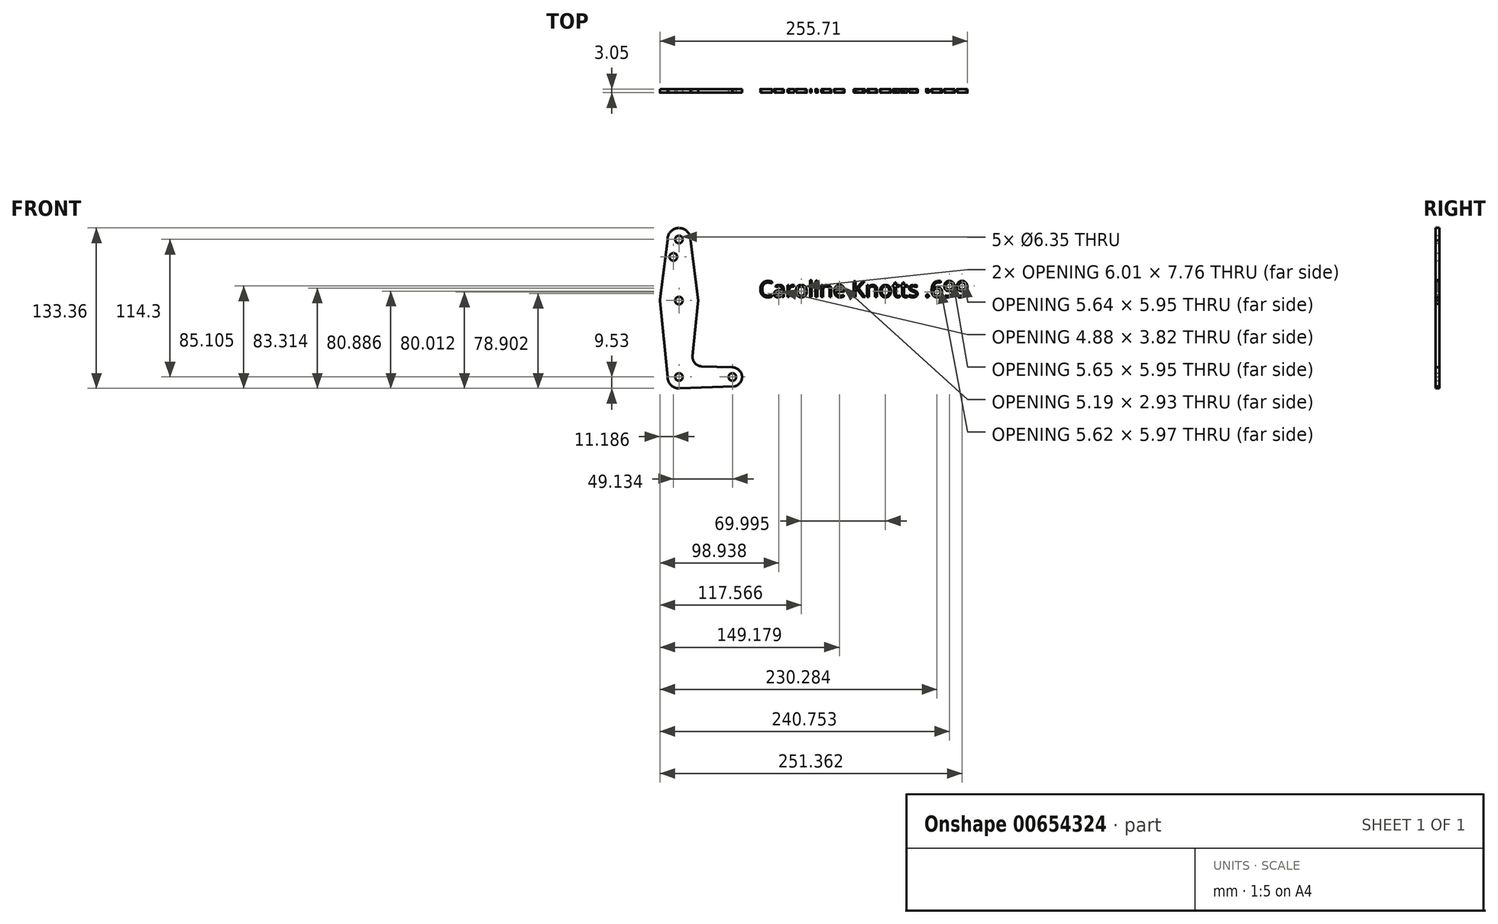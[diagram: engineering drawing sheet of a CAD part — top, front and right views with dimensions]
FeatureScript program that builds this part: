
annotation { "Feature Type Name" : "Feature", "Feature Type Description" : "" }
export const myFeature = defineFeature(function(context is Context, id is Id, definition is map)
    precondition{}
    {
        {
            var Q0;
            Q0=qCreatedBy(makeId("Front.planeOp"),FACE);
            var sketch = newSketch(context, id + "F0", { "sketchPlane" : qUnion([Q0])});
            skLineSegment(sketch, "E0", {"start": v(0, 114.3) * mm, "end": v(0, 0) * mm, "construction": true});
            skLineSegment(sketch, "E1", {"start": v(0, 0) * mm, "end": v(44.45, 0) * mm, "construction": true});
            skCircle(sketch, "E2", {"center": v(0, 63.5) * mm, "radius": 15.88 * mm});
            skCircle(sketch, "E3", {"center": v(0, 0) * mm, "radius": 9.53 * mm});
            skCircle(sketch, "E4", {"center": v(0, 114.3) * mm, "radius": 9.52 * mm});
            skCircle(sketch, "E5", {"center": v(44.45, 0) * mm, "radius": 7.94 * mm});
            skLineSegment(sketch, "E6", {"start": v(-9.52, 113.87) * mm, "end": v(-15.83, 64.73) * mm});
            skLineSegment(sketch, "E7", {"start": v(16.02, 62.56) * mm, "end": v(9.48, 113.43) * mm});
            skLineSegment(sketch, "E8", {"start": v(15.65, 60.83) * mm, "end": v(11.3, 17.59) * mm});
            skLineSegment(sketch, "E9", {"start": v(-15.87, 63.12) * mm, "end": v(-9.52, 0) * mm});
            skLineSegment(sketch, "E10", {"start": v(18.93, 8.85) * mm, "end": v(44.2, 7.93) * mm});
            skLineSegment(sketch, "E11", {"start": v(0.33, -9.52) * mm, "end": v(45.77, -7.83) * mm});
            skCircle(sketch, "E12", {"center": v(0, 114.3) * mm, "radius": 3.18 * mm});
            skCircle(sketch, "E13", {"center": v(0, 63.5) * mm, "radius": 3.18 * mm});
            skCircle(sketch, "E14", {"center": v(0, 0) * mm, "radius": 3.18 * mm});
            skCircle(sketch, "E15", {"center": v(44.45, 0) * mm, "radius": 3.18 * mm});
            skCircle(sketch, "E16", {"center": v(-4.68, 99.82) * mm, "radius": 3.18 * mm});
            skArc(sketch, "E17.filletArc", {"start": v(11.3, 17.59) * mm, "mid": v(13.23, 11.57) * mm, "end": v(18.93, 8.85) * mm});
            skText(sketch, "E18", { "text": "Caroline Knotts .699", "fontName": "OpenSans-Regular.ttf"});
            const initialGuessF0  = {"E18": [0.06649, 0.0664, 1, 0, 0.01336]};
            skSetInitialGuess(sketch, initialGuessF0);
            skSolve(sketch);
        }
        {
            var Q0;
            Q0=makeQuery(id+"F0.imprint","IMPRINT",FACE,{"disambiguationData":[TD([[makeQuery(id+"F0.imprint","IMPRINT",EDGE,{"derivedFrom":sQuery(id+"F0.wireOp",EDGE,"E16")}),-1.0]])]});
            var Q1;
            Q1=makeQuery(id+"F0.imprint","IMPRINT",FACE,{"disambiguationData":[TD([[makeQuery(id+"F0.imprint","IMPRINT",EDGE,{"derivedFrom":sQuery(id+"F0.wireOp",EDGE,"E12")}),-1.0]])]});
            var Q2;
            Q2=makeQuery(id+"F0.imprint","IMPRINT",FACE,{"disambiguationData":[TD([[makeQuery(id+"F0.imprint","IMPRINT",EDGE,{"derivedFrom":sQuery(id+"F0.wireOp",EDGE,"E13")}),-1.0]])]});
            var Q3;
            Q3=makeQuery(id+"F0.imprint","IMPRINT",FACE,{"disambiguationData":[TD([[makeQuery(id+"F0.imprint","IMPRINT",EDGE,{"derivedFrom":sQuery(id+"F0.wireOp",EDGE,"E14")}),-1.0]])]});
            var Q4;
            {var subQ6=sQuery(id+"F0.wireOp",EDGE,"E8");Q4=makeQuery(id+"F0.imprint","IMPRINT",FACE,{"disambiguationData":[TD([[makeQuery(id+"F0.imprint","IMPRINT",EDGE,{"derivedFrom":subQ6}),-1.0]])]});}
            var Q5;
            Q5=makeQuery(id+"F0.imprint","IMPRINT",FACE,{"disambiguationData":[TD([[makeQuery(id+"F0.imprint","IMPRINT",EDGE,{"derivedFrom":sQuery(id+"F0.wireOp",EDGE,"E15")}),-1.0]])]});
            var Q6;
            Q6=makeQuery(id+"F0.imprint","IMPRINT",FACE,{"disambiguationData":[TD([[makeQuery(id+"F0.imprint","IMPRINT",EDGE,{"derivedFrom":sQuery(id+"F0.wireOp",EDGE,"E18.sketch_text.stroke-15")}),-1.0]])]});
            var Q7;
            Q7=makeQuery(id+"F0.imprint","IMPRINT",FACE,{"disambiguationData":[TD([[makeQuery(id+"F0.imprint","IMPRINT",EDGE,{"derivedFrom":sQuery(id+"F0.wireOp",EDGE,"E18.sketch_text.stroke-0")}),-1.0]])]});
            var Q8;
            Q8=makeQuery(id+"F0.imprint","IMPRINT",FACE,{"disambiguationData":[TD([[makeQuery(id+"F0.imprint","IMPRINT",EDGE,{"derivedFrom":sQuery(id+"F0.wireOp",EDGE,"E18.sketch_text.stroke-42")}),-1.0]])]});
            var Q9;
            Q9=makeQuery(id+"F0.imprint","IMPRINT",FACE,{"disambiguationData":[TD([[makeQuery(id+"F0.imprint","IMPRINT",EDGE,{"derivedFrom":sQuery(id+"F0.wireOp",EDGE,"E18.sketch_text.stroke-88")}),-1.0]])]});
            var Q10;
            Q10=makeQuery(id+"F0.imprint","IMPRINT",FACE,{"disambiguationData":[TD([[makeQuery(id+"F0.imprint","IMPRINT",EDGE,{"derivedFrom":sQuery(id+"F0.wireOp",EDGE,"E18.sketch_text.stroke-105")}),-1.0]])]});
            var Q11;
            Q11=makeQuery(id+"F0.imprint","IMPRINT",FACE,{"disambiguationData":[TD([[makeQuery(id+"F0.imprint","IMPRINT",EDGE,{"derivedFrom":sQuery(id+"F0.wireOp",EDGE,"E18.sketch_text.stroke-76")}),-1.0]])]});
            var Q12;
            Q12=makeQuery(id+"F0.imprint","IMPRINT",FACE,{"disambiguationData":[TD([[makeQuery(id+"F0.imprint","IMPRINT",EDGE,{"derivedFrom":sQuery(id+"F0.wireOp",EDGE,"E18.sketch_text.stroke-80")}),-1.0]])]});
            var Q13;
            Q13=makeQuery(id+"F0.imprint","IMPRINT",FACE,{"disambiguationData":[TD([[makeQuery(id+"F0.imprint","IMPRINT",EDGE,{"derivedFrom":sQuery(id+"F0.wireOp",EDGE,"E18.sketch_text.stroke-55")}),-1.0]])]});
            var Q14;
            Q14=makeQuery(id+"F0.imprint","IMPRINT",FACE,{"disambiguationData":[TD([[makeQuery(id+"F0.imprint","IMPRINT",EDGE,{"derivedFrom":sQuery(id+"F0.wireOp",EDGE,"E18.sketch_text.stroke-72")}),-1.0]])]});
            var Q15;
            Q15=makeQuery(id+"F0.imprint","IMPRINT",FACE,{"disambiguationData":[TD([[makeQuery(id+"F0.imprint","IMPRINT",EDGE,{"derivedFrom":sQuery(id+"F0.wireOp",EDGE,"E18.sketch_text.stroke-124")}),-1.0]])]});
            var Q16;
            Q16=makeQuery(id+"F0.imprint","IMPRINT",FACE,{"disambiguationData":[TD([[makeQuery(id+"F0.imprint","IMPRINT",EDGE,{"derivedFrom":sQuery(id+"F0.wireOp",EDGE,"E18.sketch_text.stroke-136")}),-1.0]])]});
            var Q17;
            Q17=makeQuery(id+"F0.imprint","IMPRINT",FACE,{"disambiguationData":[TD([[makeQuery(id+"F0.imprint","IMPRINT",EDGE,{"derivedFrom":sQuery(id+"F0.wireOp",EDGE,"E18.sketch_text.stroke-153")}),-1.0]])]});
            var Q18;
            Q18=makeQuery(id+"F0.imprint","IMPRINT",FACE,{"disambiguationData":[TD([[makeQuery(id+"F0.imprint","IMPRINT",EDGE,{"derivedFrom":sQuery(id+"F0.wireOp",EDGE,"E18.sketch_text.stroke-241")}),-1.0]])]});
            var Q19;
            Q19=makeQuery(id+"F0.imprint","IMPRINT",FACE,{"disambiguationData":[TD([[makeQuery(id+"F0.imprint","IMPRINT",EDGE,{"derivedFrom":sQuery(id+"F0.wireOp",EDGE,"E18.sketch_text.stroke-266")}),-1.0]])]});
            var Q20;
            Q20=makeQuery(id+"F0.imprint","IMPRINT",FACE,{"disambiguationData":[TD([[makeQuery(id+"F0.imprint","IMPRINT",EDGE,{"derivedFrom":sQuery(id+"F0.wireOp",EDGE,"E18.sketch_text.stroke-189")}),-1.0]])]});
            var Q21;
            Q21=makeQuery(id+"F0.imprint","IMPRINT",FACE,{"disambiguationData":[TD([[makeQuery(id+"F0.imprint","IMPRINT",EDGE,{"derivedFrom":sQuery(id+"F0.wireOp",EDGE,"E18.sketch_text.stroke-170")}),-1.0]])]});
            var Q22;
            Q22=makeQuery(id+"F0.imprint","IMPRINT",FACE,{"disambiguationData":[TD([[makeQuery(id+"F0.imprint","IMPRINT",EDGE,{"derivedFrom":sQuery(id+"F0.wireOp",EDGE,"E18.sketch_text.stroke-208")}),-1.0]])]});
            var Q23;
            Q23=makeQuery(id+"F0.imprint","IMPRINT",FACE,{"disambiguationData":[TD([[makeQuery(id+"F0.imprint","IMPRINT",EDGE,{"derivedFrom":sQuery(id+"F0.wireOp",EDGE,"E18.sketch_text.stroke-292")}),-1.0]])]});
            var Q24;
            Q24=makeQuery(id+"F0.imprint","IMPRINT",FACE,{"disambiguationData":[TD([[makeQuery(id+"F0.imprint","IMPRINT",EDGE,{"derivedFrom":sQuery(id+"F0.wireOp",EDGE,"E18.sketch_text.stroke-233")}),-1.0]])]});
            extrude(context, id + "F1", {"entities" : qUnion([Q0, Q1, Q2, Q3, Q4, Q5, Q6, Q7, Q8, Q9, Q10, Q11, Q12, Q13, Q14, Q15, Q16, Q17, Q18, Q19, Q20, Q21, Q22, Q23, Q24]), "depth" : 3.05 * mm, "offsetDistance" : 25.4 * mm});
        }
    });
